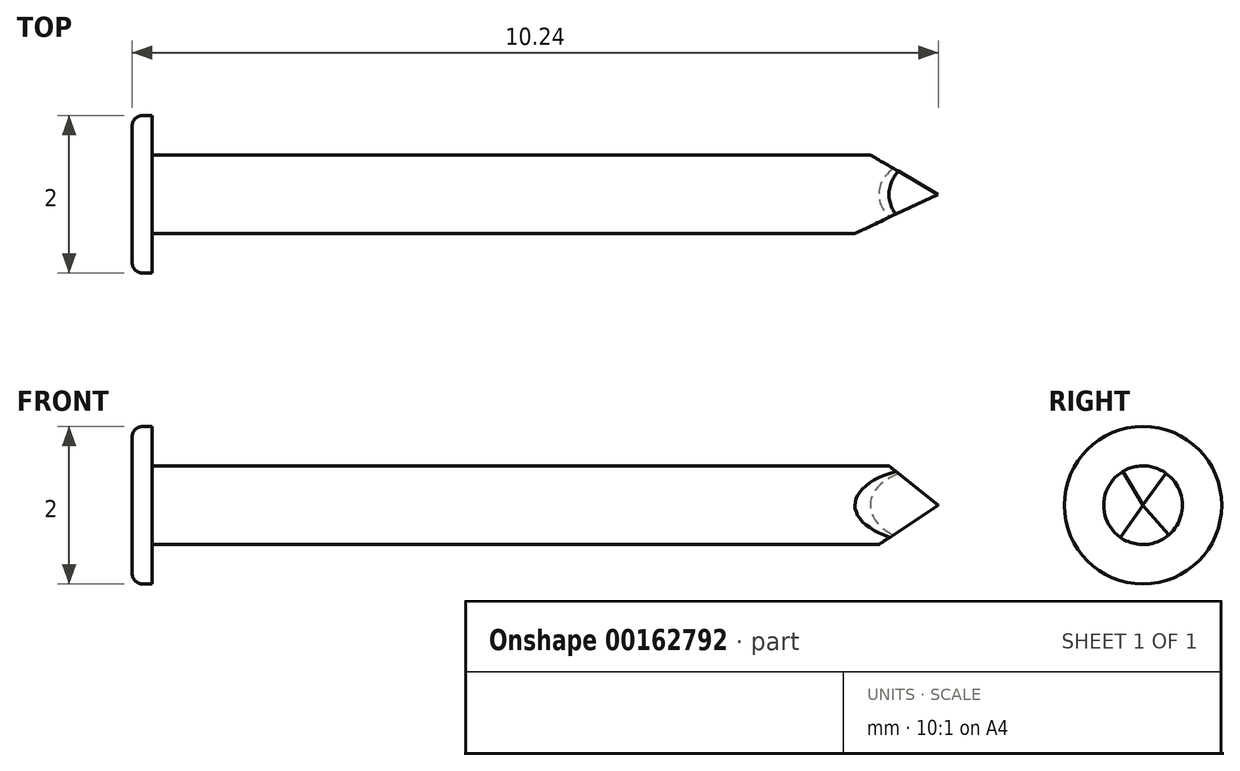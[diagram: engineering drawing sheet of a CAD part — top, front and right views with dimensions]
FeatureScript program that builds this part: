
annotation { "Feature Type Name" : "Feature", "Feature Type Description" : "" }
export const myFeature = defineFeature(function(context is Context, id is Id, definition is map)
    precondition{}
    {
        {
            var Q0;
            Q0=qCreatedBy(makeId("Right.planeOp"),FACE);
            var sketch = newSketch(context, id + "F0", { "sketchPlane" : qUnion([Q0])});
            skCircle(sketch, "E0", {"center": v(0, 0) * mm, "radius": 1 * mm});
            skCircle(sketch, "E1", {"center": v(0, 0) * mm, "radius": 0.5 * mm});
            skSolve(sketch);
        }
        {
            var Q0;
            Q0=makeQuery(id+"F0.imprint","IMPRINT",FACE,{"disambiguationData":[TD([[makeQuery(id+"F0.imprint","IMPRINT",EDGE,{"derivedFrom":sQuery(id+"F0.wireOp",EDGE,"E1")}),1.0]])]});
            var Q1;
            Q1=sQuery(id+"F0.wireOp",EDGE,"E1");
            extrude(context, id + "F1", {"entities" : qUnion([Q0]), "surfaceEntities" : qUnion([Q1]), "depth" : 10 * mm});
        }
        {
            var Q0;
            Q0=makeQuery(id+"F0.imprint","IMPRINT",FACE,{"disambiguationData":[TD([[makeQuery(id+"F0.imprint","IMPRINT",EDGE,{"derivedFrom":sQuery(id+"F0.wireOp",EDGE,"E1")}),1.0]])]});
            var Q1;
            Q1=makeQuery(id+"F0.imprint","IMPRINT",FACE,{"disambiguationData":[TD([[makeQuery(id+"F0.imprint","IMPRINT",EDGE,{"derivedFrom":sQuery(id+"F0.wireOp",EDGE,"E0")}),1.0]])]});
            extrude(context, id + "F2", {"entities" : qUnion([Q0, Q1]), "operationType" : NewBodyOperationType.ADD, "oppositeDirection" : true, "depth" : .25 * mm});
        }
        {
            var Q0;
            Q0=makeQuery(id+"F2.opExtrude","CAP_EDGE",EDGE,{"disambiguationData":[OSD([sQuery(id+"F0.wireOp",EDGE,"E0")])],"isStart":false});
            fillet(context, id + "F3", {"entities" : qUnion([Q0]), "radius" : 0.13 * mm, "tangentPropagation" : true, "allowEdgeOverflow" : false});
        }
        {
            var Q0;
            Q0=qCreatedBy(makeId("Front.planeOp"),FACE);
            var sketch = newSketch(context, id + "F4", { "sketchPlane" : qUnion([Q0])});
            skLineSegment(sketch, "E2", {"start": v(9, 0.78) * mm, "end": v(10, 0) * mm});
            skLineSegment(sketch, "E3", {"start": v(10, 0) * mm, "end": v(8.8, -0.78) * mm});
            skLineSegment(sketch, "E4", {"start": v(8.8, -0.78) * mm, "end": v(10.72, -0.75) * mm});
            skLineSegment(sketch, "E5", {"start": v(10.72, -0.75) * mm, "end": v(10.73, 1.34) * mm});
            skLineSegment(sketch, "E6", {"start": v(10.73, 1.34) * mm, "end": v(9.3, 1.2) * mm});
            skLineSegment(sketch, "E7", {"start": v(9.3, 1.2) * mm, "end": v(9, 0.78) * mm});
            skSolve(sketch);
        }
        {
            var Q0;
            Q0=makeQuery(id+"F4.imprint","IMPRINT",FACE,{"disambiguationData":[TD([[makeQuery(id+"F4.imprint","IMPRINT",EDGE,{"derivedFrom":sQuery(id+"F4.wireOp",EDGE,"E2")}),1.0]])]});
            extrude(context, id + "F5", {"entities" : qUnion([Q0]), "operationType" : NewBodyOperationType.REMOVE, "oppositeDirection" : true, "depth" : 25 * mm, "hasSecondDirection" : true, "secondDirectionOppositeDirection" : false, "secondDirectionDepth" : 25 * mm});
        }
        {
            var Q0;
            Q0=qCreatedBy(makeId("Top.planeOp"),FACE);
            var sketch = newSketch(context, id + "F6", { "sketchPlane" : qUnion([Q0])});
            skLineSegment(sketch, "E8", {"start": v(8.34, -0.78) * mm, "end": v(9.99, 0) * mm});
            skLineSegment(sketch, "E9", {"start": v(9.99, 0) * mm, "end": v(8.79, 0.7) * mm});
            skLineSegment(sketch, "E10", {"start": v(8.79, 0.7) * mm, "end": v(11.22, 0.7) * mm});
            skLineSegment(sketch, "E11", {"start": v(11.22, 0.7) * mm, "end": v(11.18, -1.21) * mm});
            skLineSegment(sketch, "E12", {"start": v(11.18, -1.21) * mm, "end": v(8.34, -0.78) * mm});
            skSolve(sketch);
        }
        {
            var Q0;
            Q0=makeQuery(id+"F6.imprint","IMPRINT",FACE,{"disambiguationData":[TD([[makeQuery(id+"F6.imprint","IMPRINT",EDGE,{"derivedFrom":sQuery(id+"F6.wireOp",EDGE,"E8")}),-1.0]])]});
            extrude(context, id + "F7", {"entities" : qUnion([Q0]), "operationType" : NewBodyOperationType.REMOVE, "depth" : 25 * mm, "hasSecondDirection" : true, "secondDirectionOppositeDirection" : true, "secondDirectionDepth" : 25 * mm});
        }
    });
